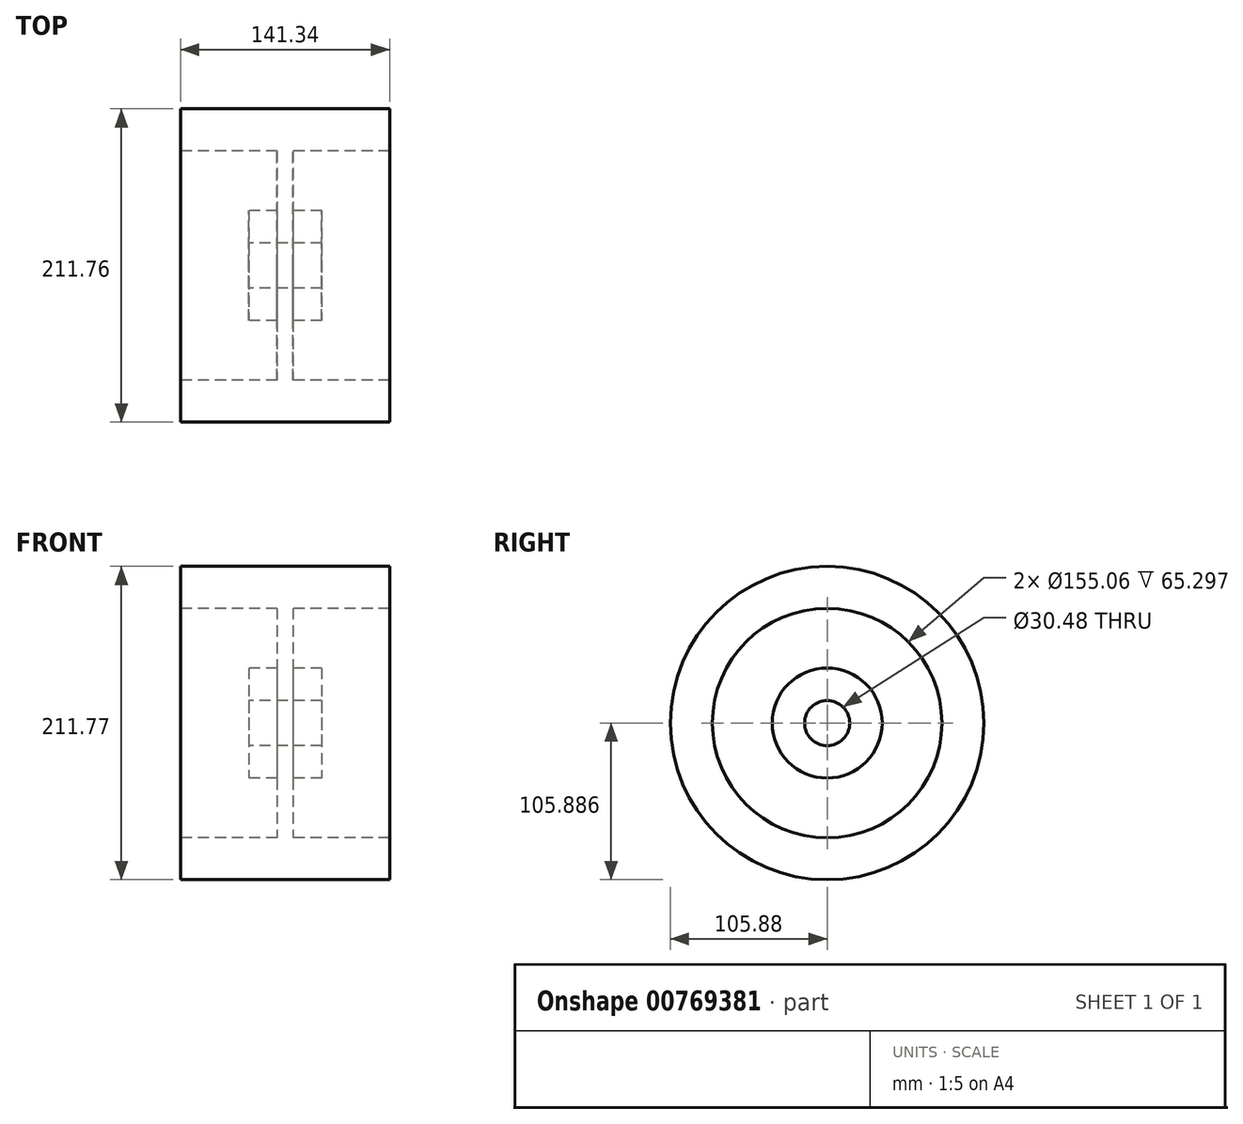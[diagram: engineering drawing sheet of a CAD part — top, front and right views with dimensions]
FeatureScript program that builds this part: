
annotation { "Feature Type Name" : "Feature", "Feature Type Description" : "" }
export const myFeature = defineFeature(function(context is Context, id is Id, definition is map)
    precondition{}
    {
        {
            var Q0;
            Q0=qCreatedBy(makeId("Front.planeOp"),FACE);
            var sketch = newSketch(context, id + "F0", { "sketchPlane" : qUnion([Q0])});
            skLineSegment(sketch, "E0.bottom", {"start": v(24.7, -10.95) * mm, "end": v(-24.7, -10.95) * mm});
            skLineSegment(sketch, "E0.top", {"start": v(24.7, 10.95) * mm, "end": v(5.37, 10.95) * mm});
            skLineSegment(sketch, "E0.left", {"start": v(24.7, -10.95) * mm, "end": v(24.7, 10.95) * mm});
            skLineSegment(sketch, "E0.right", {"start": v(-24.7, -10.95) * mm, "end": v(-24.7, 10.95) * mm});
            skPoint(sketch, "E0.middle", {"position": v(0, 0) * mm});
            skLineSegment(sketch, "E1.left", {"start": v(5.37, 10.95) * mm, "end": v(5.37, 52.2) * mm});
            skLineSegment(sketch, "E1.right", {"start": v(-5.37, 10.95) * mm, "end": v(-5.37, 52.2) * mm});
            skPoint(sketch, "E1.middle", {"position": v(0, 31.57) * mm});
            skLineSegment(sketch, "E2.bottom", {"start": v(70.67, 51.34) * mm, "end": v(5.37, 51.34) * mm});
            skLineSegment(sketch, "E2.top", {"start": v(70.67, 79.69) * mm, "end": v(-70.67, 79.69) * mm});
            skLineSegment(sketch, "E2.left", {"start": v(70.67, 51.34) * mm, "end": v(70.67, 79.69) * mm});
            skLineSegment(sketch, "E2.right", {"start": v(-70.67, 51.34) * mm, "end": v(-70.67, 79.69) * mm});
            skPoint(sketch, "E2.middle", {"position": v(0, 65.51) * mm});
            skLineSegment(sketch, "E3.trimOffspring", {"start": v(-5.37, 51.34) * mm, "end": v(-70.67, 51.34) * mm});
            skLineSegment(sketch, "E4.trimOffspring", {"start": v(-5.37, 10.95) * mm, "end": v(-24.7, 10.95) * mm});
            skSolve(sketch);
        }
        {
            var Q0;
            Q0=qCreatedBy(makeId("Right.planeOp"),FACE);
            var sketch = newSketch(context, id + "F1", { "sketchPlane" : qUnion([Q0])});
            skLineSegment(sketch, "E5", {"start": v(0, -11.17) * mm, "end": v(0, -41.43) * mm});
            skPoint(sketch, "E6.center.orphan", {"position": v(0, -26.2) * mm});
            skCircle(sketch, "E7", {"center": v(0, -26.2) * mm, "radius": 15.03 * mm});
            skSolve(sketch);
        }
        {
            var Q0;
            Q0=makeQuery(id+"F0.imprint","IMPRINT",FACE,{"disambiguationData":[TD([[makeQuery(id+"F0.imprint","IMPRINT",EDGE,{"derivedFrom":sQuery(id+"F0.wireOp",EDGE,"E0.bottom")}),-1.0]])]});
            var Q1;
            Q1=sQuery(id+"F1.wireOp",EDGE,"E7");
            revolve(context, id + "F2", {"surfaceOperationType" : NewSurfaceOperationType.NEW, "entities" : qUnion([Q0]), "axis" : qUnion([Q1]), "revolveType" : RevolveType.FULL});
        }
    });
